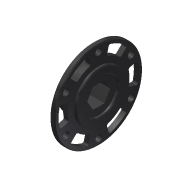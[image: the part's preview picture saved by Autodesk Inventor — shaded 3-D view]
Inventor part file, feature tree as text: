
AUTODESK INVENTOR PART (.ipt)
format: ipt  version: 2013 (Build 170138000, 138)  size: 233,472 bytes
history: native  units: in
note: dims shown in document units (in); Inventor stores cm internally (conversion verified against a paired STEP export)
features: imported_body x2, sketch x2, extrude x1, hole x1, pattern_circular x1
ambient origin geometry x8: Origin, YZ Plane, XZ Plane, XY Plane, X Axis, Y Axis, Z Axis, Center Point
feature tree (7):
  imported_body  "Imported1"
  extrude  "Extrusion1"  Depth=0.9375in
  hole  "Hole1"  [1 undecoded]
  pattern_circular  "Circular Pattern1"  [2 undecoded]
  imported_body  "Base1"
  sketch  "Sketch1"  dims[d0=1.0in d1=0.0in d2=0.9375in]
  sketch  "Sketch2"  dims[d3=0.169in d4=0.75in d5=0.375in d6=0.25in d7=0.5635in d8=1.0in d9=0.8108in d10=2.3622in d11=360.0deg]
note: 3 required parameter values undecoded (feature->parameter linkage not recoverable at this tier; creation-order binding heuristic only, values carry confidence <= 0.55)
